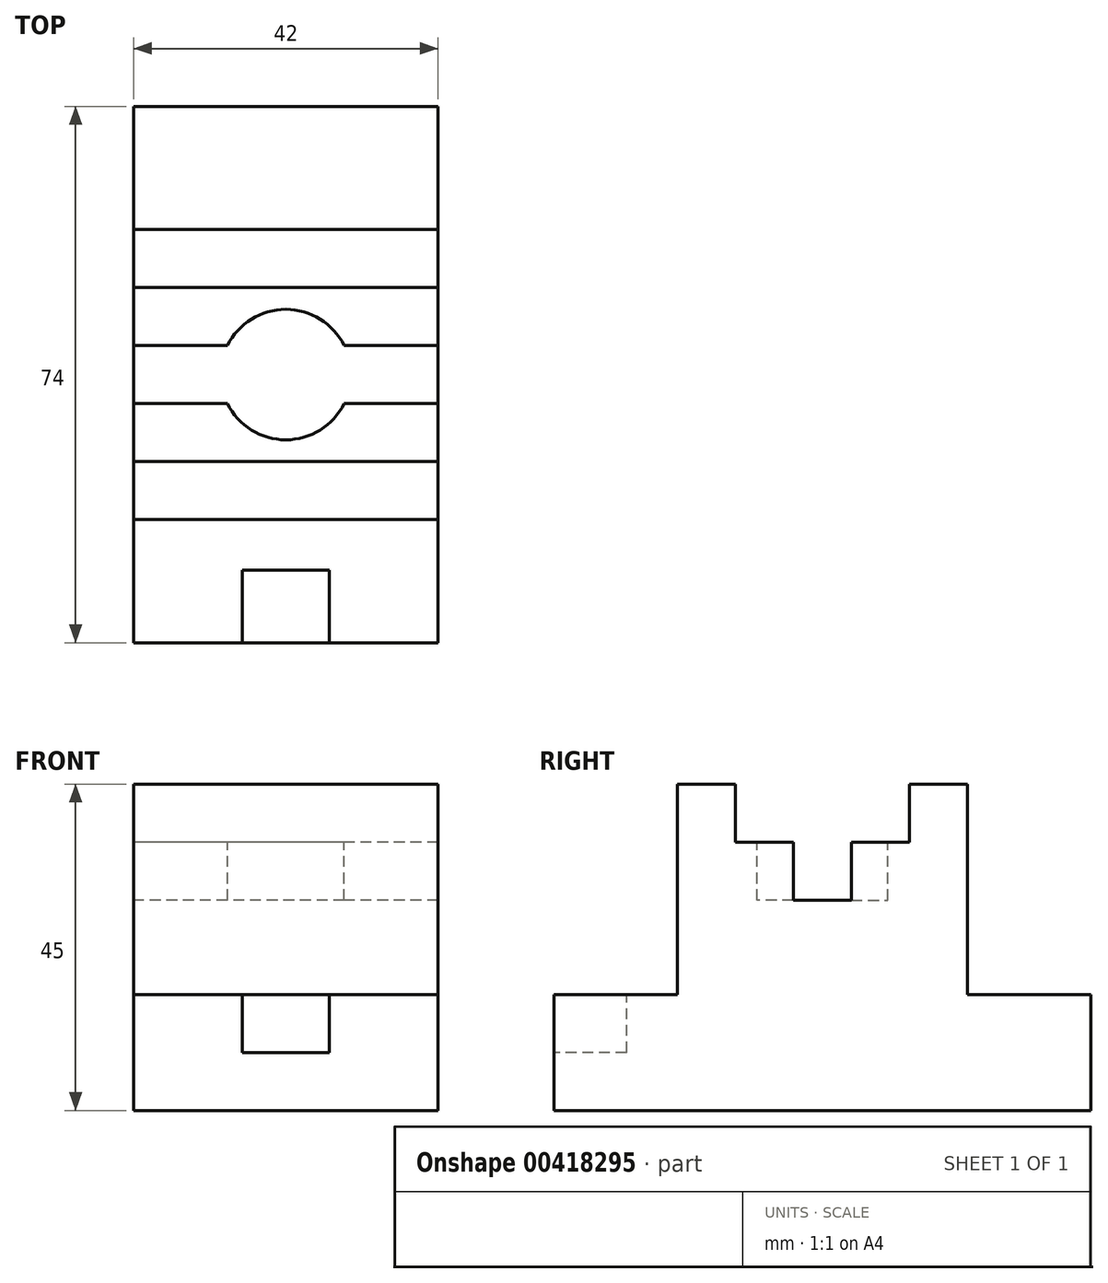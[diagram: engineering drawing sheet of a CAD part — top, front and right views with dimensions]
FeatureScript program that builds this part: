
annotation { "Feature Type Name" : "Feature", "Feature Type Description" : "" }
export const myFeature = defineFeature(function(context is Context, id is Id, definition is map)
    precondition{}
    {
        {
            var Q0;
            Q0=qCreatedBy(makeId("Right.planeOp"),FACE);
            var sketch = newSketch(context, id + "F0", { "sketchPlane" : qUnion([Q0])});
            skLineSegment(sketch, "E0", {"start": v(0, 0) * mm, "end": v(37, 0) * mm});
            skLineSegment(sketch, "E1", {"start": v(37, 0) * mm, "end": v(37, 16) * mm});
            skLineSegment(sketch, "E2", {"start": v(37, 16) * mm, "end": v(20, 16) * mm});
            skLineSegment(sketch, "E3", {"start": v(20, 16) * mm, "end": v(20, 45) * mm});
            skLineSegment(sketch, "E4", {"start": v(20, 45) * mm, "end": v(12, 45) * mm});
            skLineSegment(sketch, "E5", {"start": v(12, 45) * mm, "end": v(12, 37) * mm});
            skLineSegment(sketch, "E6", {"start": v(12, 37) * mm, "end": v(4, 37) * mm});
            skLineSegment(sketch, "E7", {"start": v(4, 37) * mm, "end": v(4, 29) * mm});
            skLineSegment(sketch, "E8", {"start": v(4, 29) * mm, "end": v(0, 29) * mm});
            skLineSegment(sketch, "E9", {"start": v(0, 29) * mm, "end": v(0, 0) * mm, "construction": true});
            skLineSegment(sketch, "E10.MirrorCS", {"start": v(-4, 29) * mm, "end": v(0, 29) * mm});
            skLineSegment(sketch, "E11.MirrorCS", {"start": v(-4, 37) * mm, "end": v(-4, 29) * mm});
            skLineSegment(sketch, "E12.MirrorCS", {"start": v(-12, 37) * mm, "end": v(-4, 37) * mm});
            skLineSegment(sketch, "E13.MirrorCS", {"start": v(-12, 45) * mm, "end": v(-12, 37) * mm});
            skLineSegment(sketch, "E14.MirrorCS", {"start": v(-20, 45) * mm, "end": v(-12, 45) * mm});
            skLineSegment(sketch, "E15.MirrorCS", {"start": v(-20, 16) * mm, "end": v(-20, 45) * mm});
            skLineSegment(sketch, "E16.MirrorCS", {"start": v(-37, 16) * mm, "end": v(-20, 16) * mm});
            skLineSegment(sketch, "E17.MirrorCS", {"start": v(-37, 0) * mm, "end": v(-37, 16) * mm});
            skLineSegment(sketch, "E18.MirrorCS", {"start": v(0, 0) * mm, "end": v(-37, 0) * mm});
            skSolve(sketch);
        }
        {
            var Q0;
            Q0 = qSketchRegion(id + "F0", true);
            extrude(context, id + "F1", {"entities" : qUnion([Q0]), "endBound" : BoundingType.SYMMETRIC, "depth" : 42 * mm});
        }
        {
            var Q0;
            Q0=makeQuery(id+"F1.opExtrude","SWEPT_FACE",FACE,{"disambiguationData":[OSD([sQuery(id+"F0.wireOp",EDGE,"E6")])]});
            var sketch = newSketch(context, id + "F2", { "sketchPlane" : qUnion([Q0])});
            skCircle(sketch, "E19", {"center": v(0, 0) * mm, "radius": 9 * mm});
            skSolve(sketch);
        }
        {
            var Q0;
            Q0 = qSketchRegion(id + "F2", true);
            var Q1;
            Q1=makeQuery(id+"F1.opExtrude","SWEPT_FACE",FACE,{"disambiguationData":[OSD([sQuery(id+"F0.wireOp",EDGE,"E8"),sQuery(id+"F0.wireOp",EDGE,"E10.MirrorCS")])]});
            extrude(context, id + "F3", {"entities" : qUnion([Q0]), "operationType" : NewBodyOperationType.REMOVE, "endBound" : BoundingType.UP_TO_SURFACE, "oppositeDirection" : true, "endBoundEntityFace" : qUnion([Q1]), "depth" : 25 * mm});
        }
        {
            var Q0;
            Q0=makeQuery(id+"F1.opExtrude","SWEPT_FACE",FACE,{"disambiguationData":[OSD([sQuery(id+"F0.wireOp",EDGE,"E16.MirrorCS")])]});
            var sketch = newSketch(context, id + "F4", { "sketchPlane" : qUnion([Q0])});
            skLineSegment(sketch, "E20.bottom", {"start": v(-6, -27) * mm, "end": v(6, -27) * mm});
            skLineSegment(sketch, "E20.top", {"start": v(-6, -37) * mm, "end": v(6, -37) * mm});
            skLineSegment(sketch, "E20.left", {"start": v(-6, -27) * mm, "end": v(-6, -37) * mm});
            skLineSegment(sketch, "E20.right", {"start": v(6, -27) * mm, "end": v(6, -37) * mm});
            skSolve(sketch);
        }
        {
            var Q0;
            Q0 = qSketchRegion(id + "F4", true);
            extrude(context, id + "F5", {"entities" : qUnion([Q0]), "operationType" : NewBodyOperationType.REMOVE, "oppositeDirection" : true, "depth" : 8 * mm});
        }
    });
